# Revit family: OHP-NRG
name_source: partatom
category: Mechanical Equipment
units: mm (PartAtom-declared; Revit-internal decimal feet)

## family parameters
Always vertical = Yes
Cut with Voids When Loaded = No
OmniClass Number = 23.40.40.11.17
OmniClass Title = Refrigerated Cases
Part Type = Normal
Room Calculation Point = No
Round Connector Dimension = Use Radius
Shared = No
Work Plane-Based = Yes

## types (12) — shared parameters
16" Shelf = Yes
18" Shelf = Yes
20" Shelf = Yes
BOTTOM ELECTRICAL = Yes
BOTTOM REFRIGERATION PIPING = Yes
Certifications = NSF 7, UL471, CSA
DATE = 05/16/2016
DESIGNERS NAME = SHIDDRAMESH
DRAIN PIPING = Yes
Default Elevation = 48"
Description = Multi-Deck Merchandiser
EQUIPMENT DESCRIPTION = Multi-Deck Merchandiser
EQUIPMENT MARK = OHP-NRG
Electric Defrost Fail-Safe = 35 (Min)
Electric Defrost Termination Temp (°F) = 47 °F
GLASS = Glass
Height = 69 1/2"
Hot Gas Defrost Fail-Safe = 26 (Min)
Hot Gas Defrost Termination Temp (°F) = 45 °F
Item Description = Multi-Deck Merchandiser
LF STD END = Yes
Legend Number = OHP-NRG
Manufacturer = HILL PHOENIX
Model = OHP-NRG
PAINTED METAL UPPER SHELF = PAINTED SHELVES
REAR REFRIGERATION PIPING = Yes
REFRIGERATION PIPING = COPPER PIPE
RT STD END = Yes
Run-Off Time (Min) = 6-8 (Min)
STAINLESS STEEL = GALVANIZED STEEL
Standard Power Amps = 0 A
Superheat Set Point @ Bulb (°F) = 6-8  °F
TOP REFRIGERATION PIPING = Yes
URL = http://www.hillphoenix.com
Width = 43 1/4"

## per-type parameters (varying)
- 04' Cut Produce: Application Discipline=Cut Produce; BTUH Conventional=950; BTUH Parallel=910; CENTER LINE=24"; DRAIN LINE=36"; Defrost (Phase 1) 208 V Amps=2 A; Defrost (Phase 1) 208 V Watts=400 W; Defrost (Phase 1) 240 V Amps=2 A; Defrost (Phase 1) 240 V Watts=532 W; Defrosts Per Day=6; Discharge Air (°F)=36 °F; Discharge Air Velocity (FPM)=150 FPM; Evaporator (°F)=32 °F; High Efficiency Amps=0 A; High Efficiency Watts=28 W; High Power (Cornice) Amps=0 A; High Power (Cornice) Watts=22 W; Length=48"; Length of Cases=48"; Light Length=4'; Lights Per Row=1; Number of Fans=2; Refgn=22 1/2"; Refgn-2=7 5/8"; Standard Power Watts=12 W; Timed-Off Defrost Fail-Safe (Min)=35 (Min); Timed-Off Defrost Termination Temp=42 °F
- 06' Cut Produce: Application Discipline=Cut Produce; BTUH Conventional=1190; BTUH Parallel=1103; CENTER LINE=36"; DRAIN LINE=36"; Defrost (Phase 1) 208 V Amps=3 A; Defrost (Phase 1) 208 V Watts=600 W; Defrost (Phase 1) 240 V Amps=3 A; Defrost (Phase 1) 240 V Watts=798 W; Defrosts Per Day=3; Discharge Air (°F)=31 °F; Discharge Air Velocity (FPM)=350 FPM; Evaporator (°F)=26 °F; High Efficiency Amps=0 A; High Efficiency Watts=28 W; High Power (Cornice) Amps=0 A; High Power (Cornice) Watts=30 W; Length=72"; Length of Cases=72"; Light Length=3'; Lights Per Row=2; Number of Fans=2; Refgn=28 5/8"; Refgn-2=8 1/2"; Standard Power Watts=17 W; Timed-Off Defrost Fail-Safe (Min)=35 (Min); Timed-Off Defrost Termination Temp=47 °F
- 08' Cut Produce: Application Discipline=Cut Produce; BTUH Conventional=950; BTUH Parallel=910; CENTER LINE=48"; DRAIN LINE=48"; Defrost (Phase 1) 208 V Amps=4 A; Defrost (Phase 1) 208 V Watts=800 W; Defrost (Phase 1) 240 V Amps=7 A; Defrost (Phase 1) 240 V Watts=1065 W; Defrosts Per Day=3; Discharge Air (°F)=36 °F; Discharge Air Velocity (FPM)=150 FPM; Evaporator (°F)=32 °F; High Efficiency Amps=1 A; High Efficiency Watts=42 W; High Power (Cornice) Amps=0 A; High Power (Cornice) Watts=43 W; Length=96"; Length of Cases=96"; Light Length=4'; Lights Per Row=2; Number of Fans=3; Refgn=28 5/8"; Refgn-2=8 1/2"; Standard Power Watts=24 W; Timed-Off Defrost Fail-Safe (Min)=35 (Min); Timed-Off Defrost Termination Temp=47 °F
- 12' Cut Produce: Application Discipline=Cut Produce; BTUH Conventional=1190; BTUH Parallel=1103; CENTER LINE=72"; DRAIN LINE=72"; Defrost (Phase 1) 208 V Amps=6 A; Defrost (Phase 1) 208 V Watts=1200 W; Defrost (Phase 1) 240 V Amps=7 A; Defrost (Phase 1) 240 V Watts=1600 W; Defrosts Per Day=3; Discharge Air (°F)=31 °F; Discharge Air Velocity (FPM)=350 FPM; Evaporator (°F)=26 °F; High Efficiency Amps=1 A; High Efficiency Watts=56 W; High Power (Cornice) Amps=1 A; High Power (Cornice) Watts=65 W; Length=144"; Length of Cases=144"; Light Length=4'; Lights Per Row=3; Number of Fans=4; Refgn=28 5/8"; Refgn-2=8 1/2"; Standard Power Watts=26 W; Timed-Off Defrost Fail-Safe (Min)=35 (Min); Timed-Off Defrost Termination Temp=47 °F
- 04' Bulk Produce: Application Discipline=Bulk Produce; BTUH Conventional=767; BTUH Parallel=735; CENTER LINE=24"; DRAIN LINE=36"; Defrost (Phase 1) 208 V Amps=2 A; Defrost (Phase 1) 208 V Watts=400 W; Defrost (Phase 1) 240 V Amps=2 A; Defrost (Phase 1) 240 V Watts=532 W; Defrosts Per Day=6; Discharge Air (°F)=38 °F; Discharge Air Velocity (FPM)=150 FPM; Evaporator (°F)=34 °F; High Efficiency Amps=0 A; High Efficiency Watts=28 W; High Power (Cornice) Amps=0 A; High Power (Cornice) Watts=22 W; Length=48"; Length of Cases=48"; Light Length=4'; Lights Per Row=1; Number of Fans=2; Refgn=22 1/2"; Refgn-2=7 5/8"; Standard Power Watts=12 W; Timed-Off Defrost Fail-Safe (Min)=42 (Min); Timed-Off Defrost Termination Temp=42 °F
- 06' Bulk Produce: Application Discipline=Bulk Produce; BTUH Conventional=801; BTUH Parallel=743; CENTER LINE=36"; DRAIN LINE=36"; Defrost (Phase 1) 208 V Amps=3 A; Defrost (Phase 1) 208 V Watts=600 W; Defrost (Phase 1) 240 V Amps=3 A; Defrost (Phase 1) 240 V Watts=798 W; Defrosts Per Day=3; Discharge Air (°F)=36 °F; Discharge Air Velocity (FPM)=250 FPM; Evaporator (°F)=29 °F; High Efficiency Amps=0 A; High Efficiency Watts=28 W; High Power (Cornice) Amps=0 A; High Power (Cornice) Watts=30 W; Length=72"; Length of Cases=72"; Light Length=3'; Lights Per Row=2; Number of Fans=2; Refgn=28 5/8"; Refgn-2=8 1/2"; Standard Power Watts=17 W; Timed-Off Defrost Fail-Safe (Min)=35 (Min); Timed-Off Defrost Termination Temp=47 °F
- 08' Bulk Produce: Application Discipline=Bulk Produce; BTUH Conventional=767; BTUH Parallel=735; CENTER LINE=48"; DRAIN LINE=48"; Defrost (Phase 1) 208 V Amps=4 A; Defrost (Phase 1) 208 V Watts=800 W; Defrost (Phase 1) 240 V Amps=7 A; Defrost (Phase 1) 240 V Watts=1065 W; Defrosts Per Day=3; Discharge Air (°F)=38 °F; Discharge Air Velocity (FPM)=150 FPM; Evaporator (°F)=34 °F; High Efficiency Amps=1 A; High Efficiency Watts=42 W; High Power (Cornice) Amps=0 A; High Power (Cornice) Watts=43 W; Length=96"; Length of Cases=96"; Light Length=4'; Lights Per Row=2; Number of Fans=3; Refgn=28 5/8"; Refgn-2=8 1/2"; Standard Power Watts=24 W; Timed-Off Defrost Fail-Safe (Min)=35 (Min); Timed-Off Defrost Termination Temp=47 °F
- 12' Bulk Produce: Application Discipline=Bulk Produce; BTUH Conventional=801; BTUH Parallel=743; CENTER LINE=72"; DRAIN LINE=72"; Defrost (Phase 1) 208 V Amps=6 A; Defrost (Phase 1) 208 V Watts=1200 W; Defrost (Phase 1) 240 V Amps=7 A; Defrost (Phase 1) 240 V Watts=1600 W; Defrosts Per Day=3; Discharge Air (°F)=36 °F; Discharge Air Velocity (FPM)=250 FPM; Evaporator (°F)=29 °F; High Efficiency Amps=1 A; High Efficiency Watts=56 W; High Power (Cornice) Amps=1 A; High Power (Cornice) Watts=65 W; Length=144"; Length of Cases=144"; Light Length=4'; Lights Per Row=3; Number of Fans=4; Refgn=28 5/8"; Refgn-2=8 1/2"; Standard Power Watts=26 W; Timed-Off Defrost Fail-Safe (Min)=35 (Min); Timed-Off Defrost Termination Temp=47 °F
- 12': Application Discipline=Bulk Produce; BTUH Conventional=801; BTUH Parallel=743; CENTER LINE=72"; DRAIN LINE=72"; Defrost (Phase 1) 208 V Amps=6 A; Defrost (Phase 1) 208 V Watts=1200 W; Defrost (Phase 1) 240 V Amps=7 A; Defrost (Phase 1) 240 V Watts=1600 W; Defrosts Per Day=3; Discharge Air (°F)=36 °F; Discharge Air Velocity (FPM)=250 FPM; Evaporator (°F)=29 °F; High Efficiency Amps=1 A; High Efficiency Watts=71 W; High Power (Cornice) Amps=0 A; High Power (Cornice) Watts=45 W; Length=144"; Length of Cases=48"; Light Length=4'; Lights Per Row=3; Number of Fans=4; Refgn=28 5/8"; Refgn-2=8 1/2"; Standard Power Watts=18 W; Timed-Off Defrost Fail-Safe (Min)=35 (Min); Timed-Off Defrost Termination Temp=47 °F
- 8': Application Discipline=Bulk Produce; BTUH Conventional=767; BTUH Parallel=735; CENTER LINE=48"; DRAIN LINE=48"; Defrost (Phase 1) 208 V Amps=4 A; Defrost (Phase 1) 208 V Watts=800 W; Defrost (Phase 1) 240 V Amps=4 A; Defrost (Phase 1) 240 V Watts=1065 W; Defrosts Per Day=3; Discharge Air (°F)=38 °F; Discharge Air Velocity (FPM)=150 FPM; Evaporator (°F)=34 °F; High Efficiency Amps=1 A; High Efficiency Watts=53 W; High Power (Cornice) Amps=0 A; High Power (Cornice) Watts=30 W; Length=96"; Length of Cases=48"; Light Length=4'; Lights Per Row=2; Number of Fans=3; Refgn=28 5/8"; Refgn-2=8 1/2"; Standard Power Watts=12 W; Timed-Off Defrost Fail-Safe (Min)=35 (Min); Timed-Off Defrost Termination Temp=47 °F
- 6': Application Discipline=Bulk Produce; BTUH Conventional=801; BTUH Parallel=743; CENTER LINE=36"; DRAIN LINE=36"; Defrost (Phase 1) 208 V Amps=3 A; Defrost (Phase 1) 208 V Watts=600 W; Defrost (Phase 1) 240 V Amps=3 A; Defrost (Phase 1) 240 V Watts=798 W; Defrosts Per Day=3; Discharge Air (°F)=36 °F; Discharge Air Velocity (FPM)=250 FPM; Evaporator (°F)=29 °F; High Efficiency Amps=0 A; High Efficiency Watts=35 W; High Power (Cornice) Amps=0 A; High Power (Cornice) Watts=24 W; Length=72"; Length of Cases=48"; Light Length=3'; Lights Per Row=2; Number of Fans=2; Refgn=28 5/8"; Refgn-2=8 1/2"; Standard Power Watts=9 W; Timed-Off Defrost Fail-Safe (Min)=35 (Min); Timed-Off Defrost Termination Temp=47 °F
- 4': Application Discipline=Cut Produce; BTUH Conventional=950; BTUH Parallel=910; CENTER LINE=24"; DRAIN LINE=36"; Defrost (Phase 1) 208 V Amps=2 A; Defrost (Phase 1) 208 V Watts=400 W; Defrost (Phase 1) 240 V Amps=2 A; Defrost (Phase 1) 240 V Watts=532 W; Defrosts Per Day=6; Discharge Air (°F)=36 °F; Discharge Air Velocity (FPM)=150 FPM; Evaporator (°F)=32 °F; High Efficiency Amps=0 A; High Efficiency Watts=0 W; High Power (Cornice) Amps=0 A; High Power (Cornice) Watts=15 W; Length=48"; Length of Cases=48"; Light Length=4'; Lights Per Row=1; Number of Fans=1; Refgn=28 5/8"; Refgn-2=7 5/8"; Standard Power Watts=6 W; Timed-Off Defrost Fail-Safe (Min)=35 (Min); Timed-Off Defrost Termination Temp=42 °F

## geometry (parser evidence)
native form markers: Blend x17, Sweep x11
no freeform markers — native parametric forms only
